SOLIDWORKS PART (.sldprt)
format: sldprt  version: not decoded by parser v0  size: 159,744 bytes
history: native  units: mm
features: sketch x5, cut_extrude x4, plane x3, fillet x2, material x1, extrude x1 (+10 scaffold rows collapsed)
feature tree (26):
  scaffold x10  (default folders/planes/origin — collapsed)
  material  "Matériau <non spécifié>"
  plane  "Plan de face"
  plane  "Plan de dessus"
  plane  "Plan de droite"
  sketch  "Esquisse1"  dims[D1=15.0mm]
  extrude  "Extrusion1"  Depth=15mm
  sketch  "Esquisse2"  dims[c1.D1=~0.519272mm c1.D2=2.2mm c2.D1=15.0mm]
  cut_extrude  "Enlèv. mat.-Extru.1"  [1 undecoded]
  sketch  "Esquisse3"  dims[D1=10.0mm D2=1.5mm D3=3.0mm D4=6.0mm D5=2.0mm D6=2.75mm D7=2.75mm]
  cut_extrude  "Enlèv. mat.-Extru.3"  Depth=1.5mm
  fillet  "Congé1"  Radius=1.49mm
  fillet  "Congé2"  Radius=1.49mm
  sketch  "Esquisse4"  dims[D2=~0.916426mm D1=25.0mm]
  cut_extrude  "Enlèv. mat.-Extru.4"  Depth=6mm
  sketch  "Esquisse5"  dims[D1=~0.608306mm]
  cut_extrude  "Enlèv. mat.-Extru.5"  Depth=6mm
decode coverage: 11 of 12 modeling features carry decoded parameters
note: ~ marks probable driven/reference dimensions
note: 1 parameter value undecoded
note: suppression state not decoded; provenance and decode notes live in map.json
